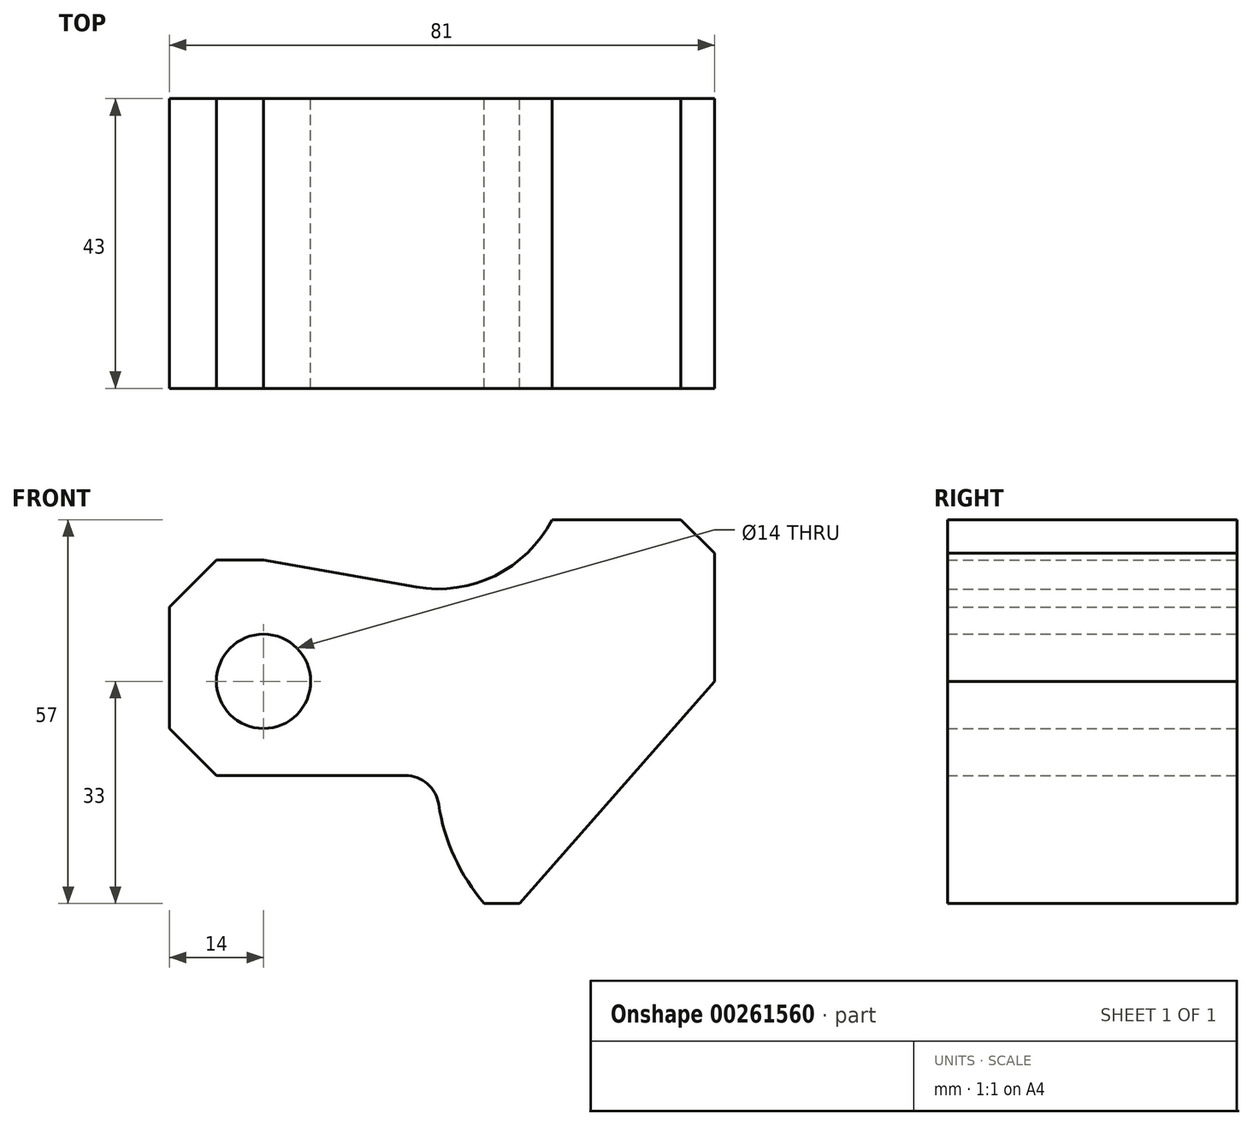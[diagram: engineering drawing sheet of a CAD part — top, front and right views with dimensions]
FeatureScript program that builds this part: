
annotation { "Feature Type Name" : "Feature", "Feature Type Description" : "" }
export const myFeature = defineFeature(function(context is Context, id is Id, definition is map)
    precondition{}
    {
        {
            var Q0;
            Q0=qCreatedBy(makeId("Front.planeOp"),FACE);
            var sketch = newSketch(context, id + "F0", { "sketchPlane" : qUnion([Q0])});
            skLineSegment(sketch, "E0", {"start": v(0, 0) * mm, "end": v(0, 18) * mm});
            skLineSegment(sketch, "E1", {"start": v(0, 0) * mm, "end": v(0, -7) * mm, "construction": true});
            skLineSegment(sketch, "E2", {"start": v(0, -7) * mm, "end": v(7, -7) * mm, "construction": true});
            skLineSegment(sketch, "E3", {"start": v(7, -7) * mm, "end": v(0, 0) * mm});
            skLineSegment(sketch, "E4", {"start": v(0, 18) * mm, "end": v(0, 25) * mm, "construction": true});
            skLineSegment(sketch, "E5", {"start": v(0, 25) * mm, "end": v(7, 25) * mm, "construction": true});
            skLineSegment(sketch, "E6", {"start": v(7, 25) * mm, "end": v(0, 18) * mm});
            skLineSegment(sketch, "E7", {"start": v(7, 25) * mm, "end": v(14, 25) * mm});
            skLineSegment(sketch, "E8", {"start": v(7, -7) * mm, "end": v(14, -7) * mm});
            skLineSegment(sketch, "E9", {"start": v(14, -7) * mm, "end": v(14, 7) * mm, "construction": true});
            skCircle(sketch, "E10", {"center": v(14, 7) * mm, "radius": 7 * mm});
            skLineSegment(sketch, "E11", {"start": v(14, -7) * mm, "end": v(35.07, -7) * mm});
            skLineSegment(sketch, "E12", {"start": v(14, 25) * mm, "end": v(36.65, 21) * mm});
            skLineSegment(sketch, "E13", {"start": v(14, 7) * mm, "end": v(81, 7) * mm, "construction": true});
            skLineSegment(sketch, "E14", {"start": v(14, 7) * mm, "end": v(0, 7) * mm, "construction": true});
            skLineSegment(sketch, "E15", {"start": v(81, 7) * mm, "end": v(81, 26) * mm});
            skLineSegment(sketch, "E16", {"start": v(81, 26) * mm, "end": v(71.14, 26) * mm, "construction": true});
            skLineSegment(sketch, "E17", {"start": v(81, 26) * mm, "end": v(76, 31) * mm});
            skLineSegment(sketch, "E18", {"start": v(76, 31) * mm, "end": v(56.83, 31) * mm});
            skLineSegment(sketch, "E19", {"start": v(81, 7) * mm, "end": v(81, -26) * mm, "construction": true});
            skLineSegment(sketch, "E20", {"start": v(81, -26) * mm, "end": v(52, -26) * mm, "construction": true});
            skLineSegment(sketch, "E21", {"start": v(81, 7) * mm, "end": v(52, -26) * mm});
            skLineSegment(sketch, "E22", {"start": v(52, -26) * mm, "end": v(46.79, -26) * mm});
            skArc(sketch, "E23", {"start": v(36.65, 21) * mm, "mid": v(48.38, 22.7) * mm, "end": v(56.83, 31) * mm});
            skArc(sketch, "E24", {"start": v(35.07, -7) * mm, "mid": v(38.33, -8.21) * mm, "end": v(40.01, -11.26) * mm});
            skLineSegment(sketch, "E25", {"start": v(68.7, -26) * mm, "end": v(68.7, -7) * mm, "construction": true});
            skArc(sketch, "E26", {"start": v(40.01, -11.26) * mm, "mid": v(42.35, -19.12) * mm, "end": v(46.79, -26) * mm});
            skSolve(sketch);
        }
        {
            var Q0;
            Q0 = qSketchRegion(id + "F0", true);
            extrude(context, id + "F1", {"entities" : qUnion([Q0]), "depth" : 43 * mm});
        }
    });
